# Revit family: 2055961
name_source: partatom
category: Lighting Fixtures
revit_build: Autodesk Revit 2016 (Build: 20150220_1215(x64)
units: mm (PartAtom-declared; Revit-internal decimal feet)

## family parameters
Cut with Voids When Loaded = No
Host = Face
Light Source = No
OmniClass Number = 23.80.70.00
OmniClass Title = Lighting
Part Type = Normal
Room Calculation Point = No
Round Connector Dimension = Use Diameter
Shared = No

## types (1)
- 2055961 BCON PRJ FRAM O/B SM 3K BLK
    Apparent Load = 35 VA
    Assembly Code = D5020200
    AssetType = Fixed
    ClassificationName = Uniclass2015
    ClassificationValue = EF_70_80
    Cost = 0 $
    Default Elevation = 1219 mm
    Description = Beacon Projector offers precision light exactly where it is needed. The Framing Projector has four adjustable arms allowing the beam to be framed to the desired size shape (square/rectangle or irregular 4 sided shapes).High colour rendering CRI 97 typical. IR/UV free light source without heat radiation. LED technology provides an energy efficient solution with reduced maintenance costs.
    DocumentationLiterature = http://www.sylvania-lighting.com
    ElectricShockClassification = Class II
    IfcExportAs = IfcLightFixtureType
    IfcExportType = IfcLightFixtureType
    ImpactProtectionIndex = IK02
    IngressProtection = IP20
    InputNominalFrequency = 50/60 Hz
    InputVoltage = AC 230 V
    Keynote = 16500
    Lamp = LED
    LampColourRenderingIndex = 97
    LampColourTemperature = 3000 K
    LampMacAdamStep = 3
    LampNominalLuminous = 474 lm
    LampsType = LED
    LightOutputRatio = 100
    LuminousEfficacy = 14 lm/W
    Manufacturer = Feilo Sylvania
    ManufacturerName = Feilo Sylvania
    Material = aluminium housing
    Material_1_SYL = Body-Sylvania-Black
    Material_2_SYL = Body-Sylvania-Black
    Material_3_SYL = <By Category>
    Material_4_SYL = <By Category>
    Model = BCON PRJ FRAM O/B SM 3K BLK
    ModelNumber = 2055961
    ModelReference = BCON PRJ FRAM O/B SM 3K BLK
    Name = BCON PRJ FRAM O/B SM 3K BLK
    NominalDepth = 185 mm  [stored 0.606955 ft]
    NominalHeight = 215 mm
    NominalLength = 0 mm  [stored 0 ft]
    PowerConsumption = 35 W
    PowerFactor = 0.95
    Surface_SYL = Yes
    Track_SYL = No
    Type Image = <None>
    TypeHead_SYL = Beacon LED Projector Framing Head : 2055961 BCON PRJ FRAM O/B SM 3K BLK
    TypeName = BCON PRJ FRAM O/B SM 3K BLK
    URL = http://www.sylvania-lighting.com
    Voltage = 230 V
    Weight = 1.365 kg

note: [stored X ft] marks values corroborated as IEEE doubles in the binary element streams (Revit-internal decimal feet)

## geometry (parser evidence)
native form markers: Sweep x9
no freeform markers — native parametric forms only
